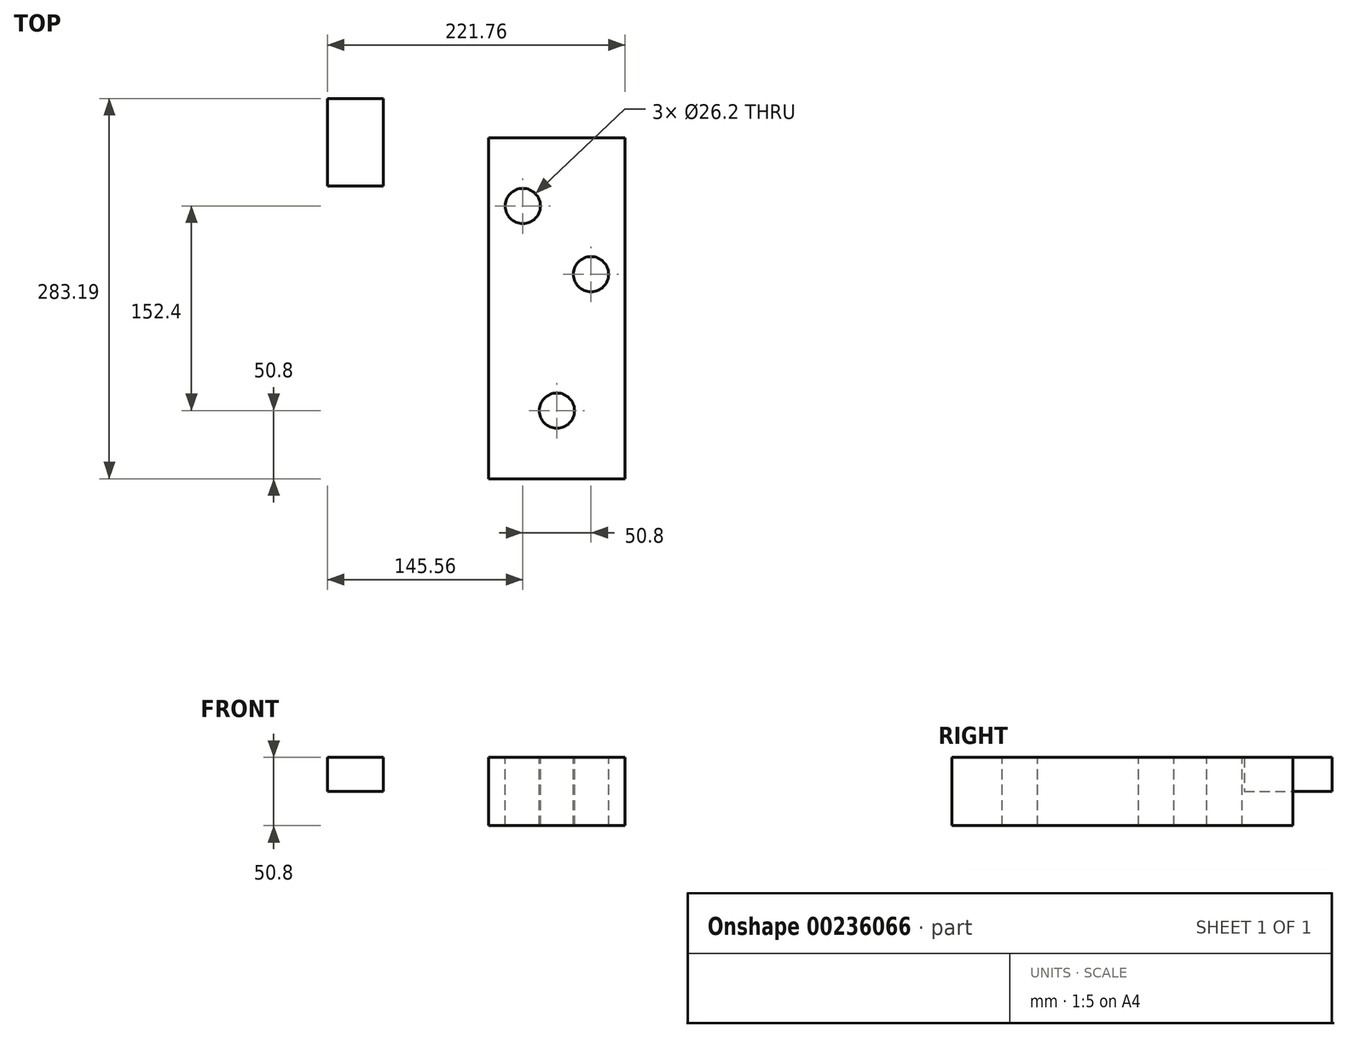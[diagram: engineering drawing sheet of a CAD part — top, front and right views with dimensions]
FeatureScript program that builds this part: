
annotation { "Feature Type Name" : "Feature", "Feature Type Description" : "" }
export const myFeature = defineFeature(function(context is Context, id is Id, definition is map)
    precondition{}
    {
        {
            var Q0;
            Q0=qCreatedBy(makeId("Front.planeOp"),FACE);
            var sketch = newSketch(context, id + "F0", { "sketchPlane" : qUnion([Q0])});
            skLineSegment(sketch, "E0", {"start": v(-50.8, 25.4) * mm, "end": v(-50.8, -25.4) * mm});
            skLineSegment(sketch, "E1", {"start": v(-50.8, -25.4) * mm, "end": v(50.8, -25.4) * mm});
            skLineSegment(sketch, "E2", {"start": v(50.8, -25.4) * mm, "end": v(50.8, 25.4) * mm});
            skLineSegment(sketch, "E3", {"start": v(50.8, 25.4) * mm, "end": v(-50.8, 25.4) * mm});
            skSolve(sketch);
        }
        {
            var Q0;
            Q0=makeQuery(id+"F0.imprint","IMPRINT",FACE,{"disambiguationData":[TD([[makeQuery(id+"F0.imprint","IMPRINT",EDGE,{"derivedFrom":sQuery(id+"F0.wireOp",EDGE,"E0")}),1.0]])]});
            var Q1;
            Q1=sQuery(id+"F0.wireOp",EDGE,"E3");
            extrude(context, id + "F1", {"entities" : qUnion([Q0]), "surfaceEntities" : qUnion([Q1]), "depth" : 254 * mm});
        }
        {
            var Q0;
            Q0=qCreatedBy(makeId("Top.planeOp"),FACE);
            var sketch = newSketch(context, id + "F2", { "sketchPlane" : qUnion([Q0])});
            skLineSegment(sketch, "E4.bottom", {"start": v(-170.96, -36.06) * mm, "end": v(-129.41, -36.06) * mm});
            skLineSegment(sketch, "E4.top", {"start": v(-170.96, 29.19) * mm, "end": v(-129.41, 29.19) * mm});
            skLineSegment(sketch, "E4.left", {"start": v(-170.96, -36.06) * mm, "end": v(-170.96, 29.19) * mm});
            skLineSegment(sketch, "E4.right", {"start": v(-129.41, -36.06) * mm, "end": v(-129.41, 29.19) * mm});
            skSolve(sketch);
        }
        {
            var Q0;
            Q0 = qSketchRegion(id + "F2", true);
            extrude(context, id + "F3", {"entities" : qUnion([Q0]), "depth" : 25.4 * mm});
        }
        {
            var Q0;
            Q0=makeQuery(id+"F1.opExtrude","SWEPT_FACE",FACE,{"disambiguationData":[OSD([sQuery(id+"F0.wireOp",EDGE,"E3")])]});
            var Q1;
            Q1=makeQuery(id+"F1.opExtrude","SWEPT_FACE",FACE,{"disambiguationData":[OSD([sQuery(id+"F0.wireOp",EDGE,"E3")])]});
            var sketch = newSketch(context, id + "F4", { "sketchPlane" : qUnion([Q0, Q1])});
            skPoint(sketch, "E5", {"position": v(0, -203.2) * mm});
            skPoint(sketch, "E6", {"position": v(-25.4, -50.8) * mm});
            skPoint(sketch, "E7", {"position": v(25.4, -101.6) * mm});
            skSolve(sketch);
        }
        {
            var Q0;
            Q0=sQuery(id+"F4.wireOp",VERTEX,"E5");
            var Q1;
            Q1=sQuery(id+"F4.wireOp",VERTEX,"E7");
            var Q2;
            Q2=sQuery(id+"F4.wireOp",VERTEX,"E6");
            var Q3;
            Q3=makeQuery(id+"F1.opExtrude","SWEPT_BODY",BODY,{"disambiguationData":[OSD([sQuery(id+"F0.wireOp",EDGE,"E0"),sQuery(id+"F0.wireOp",EDGE,"E1"),sQuery(id+"F0.wireOp",EDGE,"E2"),sQuery(id+"F0.wireOp",EDGE,"E3")])]});
            hole(context, id + "F5", {"style" : HoleStyle.SIMPLE, "endStyle" : HoleEndStyle.THROUGH, "standardTappedOrClearance" : lookupTablePath({ "standard" : "ANSI", "fit" : "Normal (ASME)", "size" : "1", "type" : "Clearance" }), "standardBlindInLast" : lookupTablePath({ "fit" : "Free", "standard" : "ANSI", "size" : "1", "type" : "Clearance" }), "holeDiameter" : 26.2 * mm, "locations" : qUnion([Q0, Q1, Q2]), "scope" : qUnion([Q3]), "isTappedThrough" : true});
        }
    });
